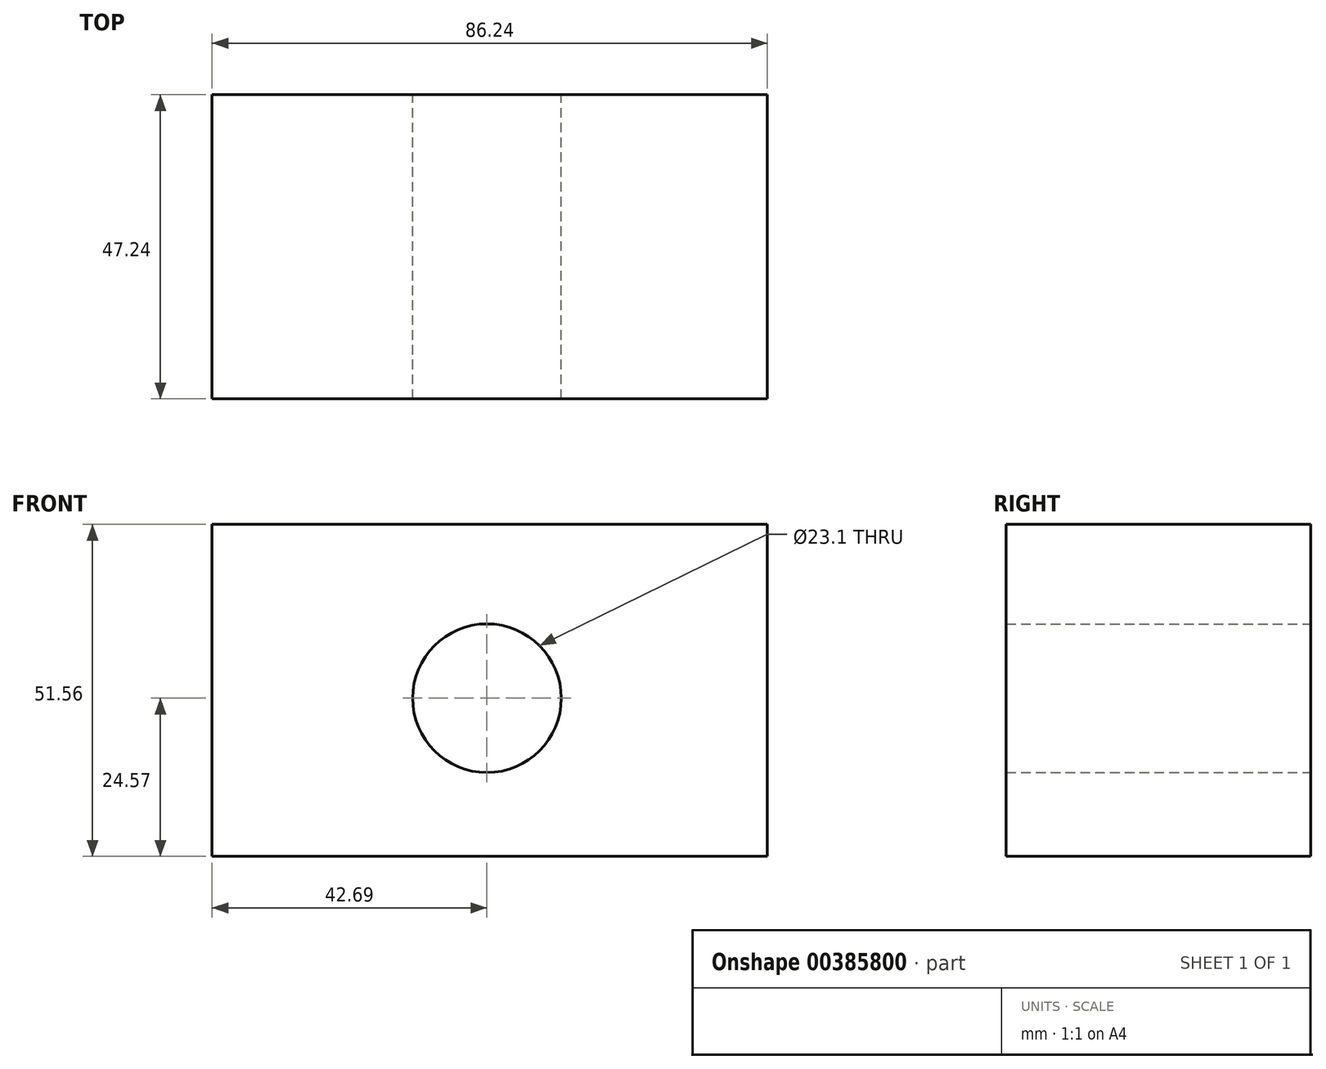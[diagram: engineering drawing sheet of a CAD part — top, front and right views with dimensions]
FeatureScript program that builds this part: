
annotation { "Feature Type Name" : "Feature", "Feature Type Description" : "" }
export const myFeature = defineFeature(function(context is Context, id is Id, definition is map)
    precondition{}
    {
        {
            var Q0;
            Q0=qCreatedBy(makeId("Front.planeOp"),FACE);
            var sketch = newSketch(context, id + "F0", { "sketchPlane" : qUnion([Q0])});
            skLineSegment(sketch, "E0.bottom", {"start": v(-42.7, 26.99) * mm, "end": v(43.55, 26.99) * mm});
            skLineSegment(sketch, "E0.top", {"start": v(-42.7, -24.57) * mm, "end": v(43.55, -24.57) * mm});
            skLineSegment(sketch, "E0.left", {"start": v(-42.7, 26.99) * mm, "end": v(-42.7, -24.57) * mm});
            skLineSegment(sketch, "E0.right", {"start": v(43.55, 26.99) * mm, "end": v(43.55, -24.57) * mm});
            skCircle(sketch, "E1", {"center": v(0, 0) * mm, "radius": 11.55 * mm});
            skSolve(sketch);
        }
        {
            var Q0;
            Q0 = qSketchRegion(id + "F0", true);
            extrude(context, id + "F1", {"entities" : qUnion([Q0]), "depth" : 47.24 * mm});
        }
    });
